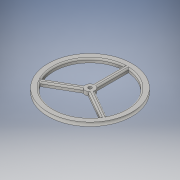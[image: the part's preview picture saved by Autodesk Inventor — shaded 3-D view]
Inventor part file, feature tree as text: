
AUTODESK INVENTOR PART (.ipt)
format: ipt  version: 2016 (Build 200138000, 138)  size: 189,952 bytes
history: native  units: in
note: dims shown in document units (in); Inventor stores cm internally (conversion verified against a paired STEP export)
features: fillet x2, sketch x2, revolve x1, extrude x1
ambient origin geometry x8: Origin, YZ Plane, XZ Plane, XY Plane, X Axis, Y Axis, Z Axis, Center Point
bodies: Solid1 (feature_tree)
feature tree (6):
  revolve  "Revolution1"  Angle=90.0deg
  extrude  "Extrusion1"  Depth=0.06in
  fillet  "Fillet1"  Radius=0.06in
  fillet  "Fillet4"  [1 undecoded]
  sketch  "Sketch1"  dims[d3=0.07in d5=90.0deg]
  sketch  "Sketch2"  dims[d14=1.0in d15=0.0in d16=0.06in d19=0.06in]
note: 1 required parameter value undecoded (feature->parameter linkage not recoverable at this tier; creation-order binding heuristic only, values carry confidence <= 0.55)
